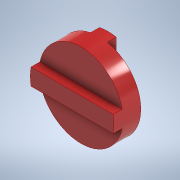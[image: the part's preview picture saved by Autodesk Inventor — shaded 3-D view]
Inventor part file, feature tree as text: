
AUTODESK INVENTOR PART (.ipt)
format: ipt  version: 2020 (Build 240168000, 168)  size: 130,048 bytes
history: native  units: in
note: dims shown in document units (in); Inventor stores cm internally (conversion verified against a paired STEP export)
features: extrude x4, sketch x4
ambient origin geometry x8: Origin, YZ Plane, XZ Plane, XY Plane, X Axis, Y Axis, Z Axis, Center Point
bodies: Solid1 (feature_tree)
feature tree (8):
  extrude  "Extrusion1"  Depth=1.1811in
  extrude  "Extrusion2"  Depth=1.2598in TaperAngle=0.0deg
  extrude  "Extrusion3"  Depth=1.1811in
  extrude  "Extrusion4"  Depth=2.9528in
  sketch  "Sketch1"  dims[d0=5.9055in d1=1.1811in d2=0.5906in]
  sketch  "Sketch2"  dims[d3=0.6299in d4=0.0in d5=1.2598in d6=0.0in]
  sketch  "Sketch3"  dims[d7=1.1811in d8=0.5906in]
  sketch  "Sketch4"  dims[d9=2.9528in d10=2.9528in d11=1.2598in d12=0.0in d17=0.6299in d18=0.0in d13=0.0197in d14=0.0344in d15=0.0197in d16=0.0344in]
